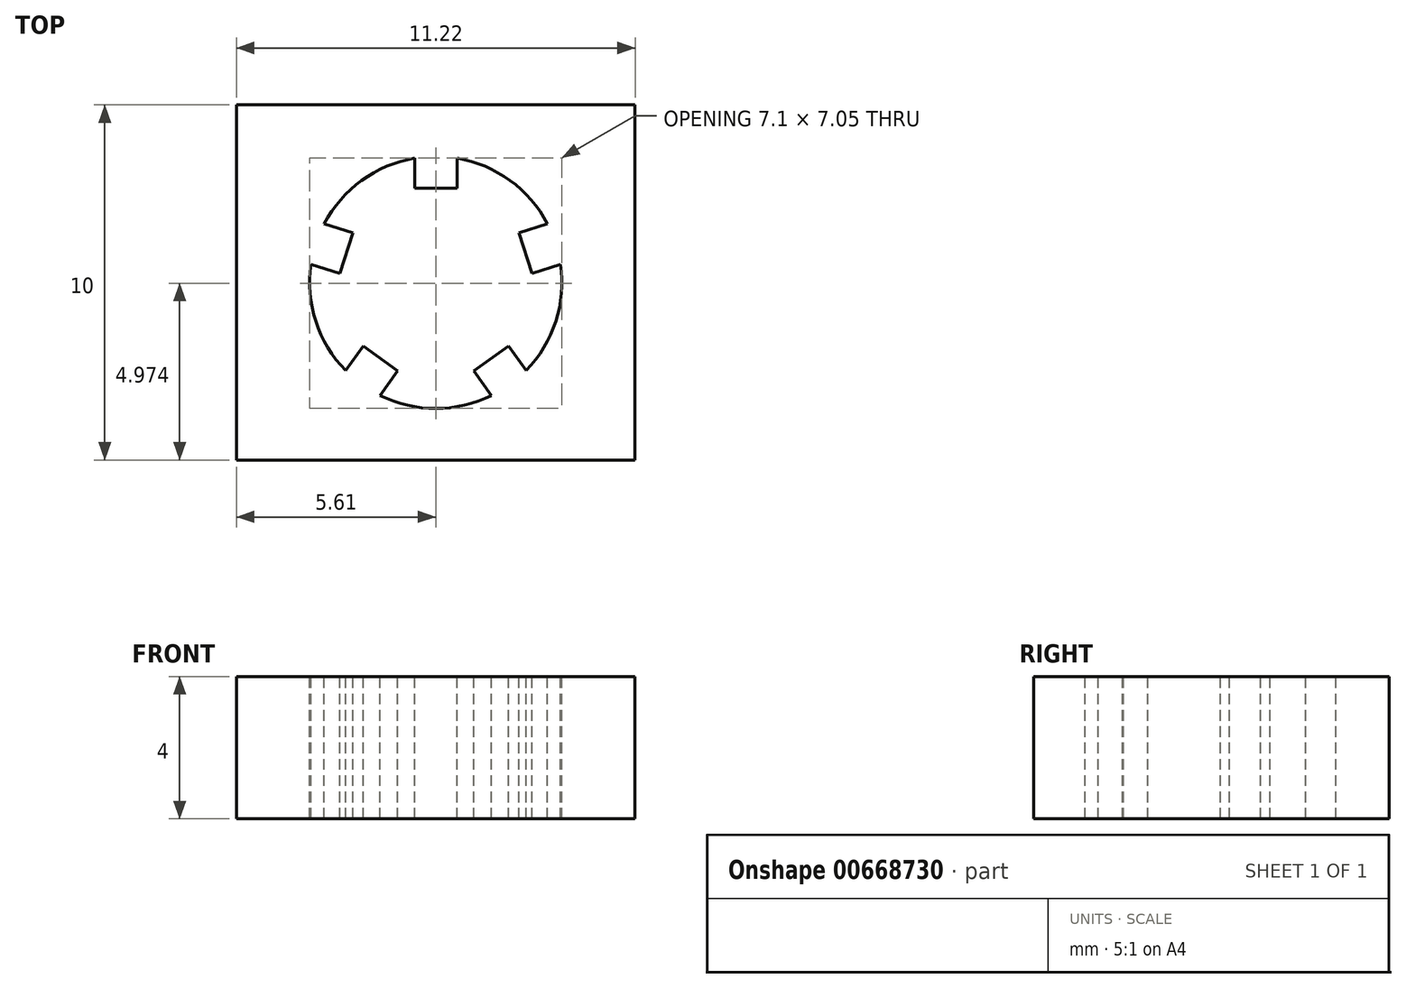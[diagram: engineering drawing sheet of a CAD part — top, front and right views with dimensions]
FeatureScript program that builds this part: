
annotation { "Feature Type Name" : "Feature", "Feature Type Description" : "" }
export const myFeature = defineFeature(function(context is Context, id is Id, definition is map)
    precondition{}
    {
        {
            assignVariable(context, id + "F0", {"name" : "Depth", "anyValue" : 4 * mm});
        }
        {
            var Q0;
            Q0=qCreatedBy(makeId("Top.planeOp"),FACE);
            var sketch = newSketch(context, id + "F1", { "sketchPlane" : qUnion([Q0])});
            skLineSegment(sketch, "E0.bottom", {"start": v(-5.6, 5) * mm, "end": v(5.6, 5) * mm});
            skLineSegment(sketch, "E0.top", {"start": v(-5.6, -5) * mm, "end": v(5.6, -5) * mm});
            skLineSegment(sketch, "E0.left", {"start": v(-5.6, 5) * mm, "end": v(-5.6, -5) * mm});
            skLineSegment(sketch, "E0.right", {"start": v(5.6, 5) * mm, "end": v(5.6, -5) * mm});
            skPoint(sketch, "E0.middle", {"position": v(0, 0) * mm});
            skSolve(sketch);
        }
        {
            var Q0;
            Q0=makeQuery(id+"F1.imprint","IMPRINT",FACE,{"disambiguationData":[TD([[makeQuery(id+"F1.imprint","IMPRINT",EDGE,{"derivedFrom":sQuery(id+"F1.wireOp",EDGE,"E0.bottom")}),-1.0]])]});
            extrude(context, id + "F2", {"entities" : qUnion([Q0]), "oppositeDirection" : true, "depth" : getVariable(context, 'Depth'), "offsetDistance" : 25 * mm});
        }
        {
            var Q0;
            Q0=qCreatedBy(makeId("Top.planeOp"),FACE);
            var sketch = newSketch(context, id + "F3", { "sketchPlane" : qUnion([Q0])});
            skCircle(sketch, "E1", {"center": v(0, 0) * mm, "radius": 3.55 * mm});
            skLineSegment(sketch, "E2", {"start": v(0, 0) * mm, "end": v(0, 3.55) * mm, "construction": true});
            skLineSegment(sketch, "E3.bottom", {"start": v(-0.6, 3.55) * mm, "end": v(0.6, 3.55) * mm});
            skLineSegment(sketch, "E3.top", {"start": v(-0.6, 2.65) * mm, "end": v(0.6, 2.65) * mm});
            skLineSegment(sketch, "E3.left", {"start": v(-0.6, 3.55) * mm, "end": v(-0.6, 2.65) * mm});
            skLineSegment(sketch, "E3.right", {"start": v(0.6, 3.55) * mm, "end": v(0.6, 2.65) * mm});
            skLineSegment(sketch, "E4.1.0", {"start": v(-3.2, 1.67) * mm, "end": v(-2.33, 1.39) * mm});
            skLineSegment(sketch, "E4.1.1", {"start": v(-3.56, 0.53) * mm, "end": v(-2.7, 0.25) * mm});
            skLineSegment(sketch, "E4.1.2", {"start": v(-2.7, 0.25) * mm, "end": v(-2.33, 1.39) * mm});
            skLineSegment(sketch, "E4.1.3", {"start": v(-3.56, 0.53) * mm, "end": v(-3.2, 1.67) * mm});
            skLineSegment(sketch, "E4.2.0", {"start": v(-2.57, -2.52) * mm, "end": v(-2.04, -1.8) * mm});
            skLineSegment(sketch, "E4.2.1", {"start": v(-1.6, -3.22) * mm, "end": v(-1.07, -2.5) * mm});
            skLineSegment(sketch, "E4.2.2", {"start": v(-1.07, -2.5) * mm, "end": v(-2.04, -1.8) * mm});
            skLineSegment(sketch, "E4.2.3", {"start": v(-1.6, -3.22) * mm, "end": v(-2.57, -2.52) * mm});
            skLineSegment(sketch, "E4.3.0", {"start": v(1.6, -3.22) * mm, "end": v(1.07, -2.5) * mm});
            skLineSegment(sketch, "E4.3.1", {"start": v(2.57, -2.52) * mm, "end": v(2.04, -1.8) * mm});
            skLineSegment(sketch, "E4.3.2", {"start": v(2.04, -1.8) * mm, "end": v(1.07, -2.5) * mm});
            skLineSegment(sketch, "E4.3.3", {"start": v(2.57, -2.52) * mm, "end": v(1.6, -3.22) * mm});
            skLineSegment(sketch, "E4.4.0", {"start": v(3.56, 0.53) * mm, "end": v(2.7, 0.25) * mm});
            skLineSegment(sketch, "E4.4.1", {"start": v(3.2, 1.67) * mm, "end": v(2.33, 1.39) * mm});
            skLineSegment(sketch, "E4.4.2", {"start": v(2.33, 1.39) * mm, "end": v(2.7, 0.25) * mm});
            skLineSegment(sketch, "E4.4.3", {"start": v(3.2, 1.67) * mm, "end": v(3.56, 0.53) * mm});
            skSolve(sketch);
        }
        {
            var Q0;
            Q0=makeQuery(id+"F3.imprint","IMPRINT",FACE,{"disambiguationData":[TD([[makeQuery(id+"F3.imprint","IMPRINT",EDGE,{"derivedFrom":sQuery(id+"F3.wireOp",EDGE,"E1")}),1.0]])]});
            extrude(context, id + "F4", {"entities" : qUnion([Q0]), "operationType" : NewBodyOperationType.REMOVE, "oppositeDirection" : true, "depth" : getVariable(context, 'Depth'), "offsetDistance" : 25 * mm});
        }
    });
